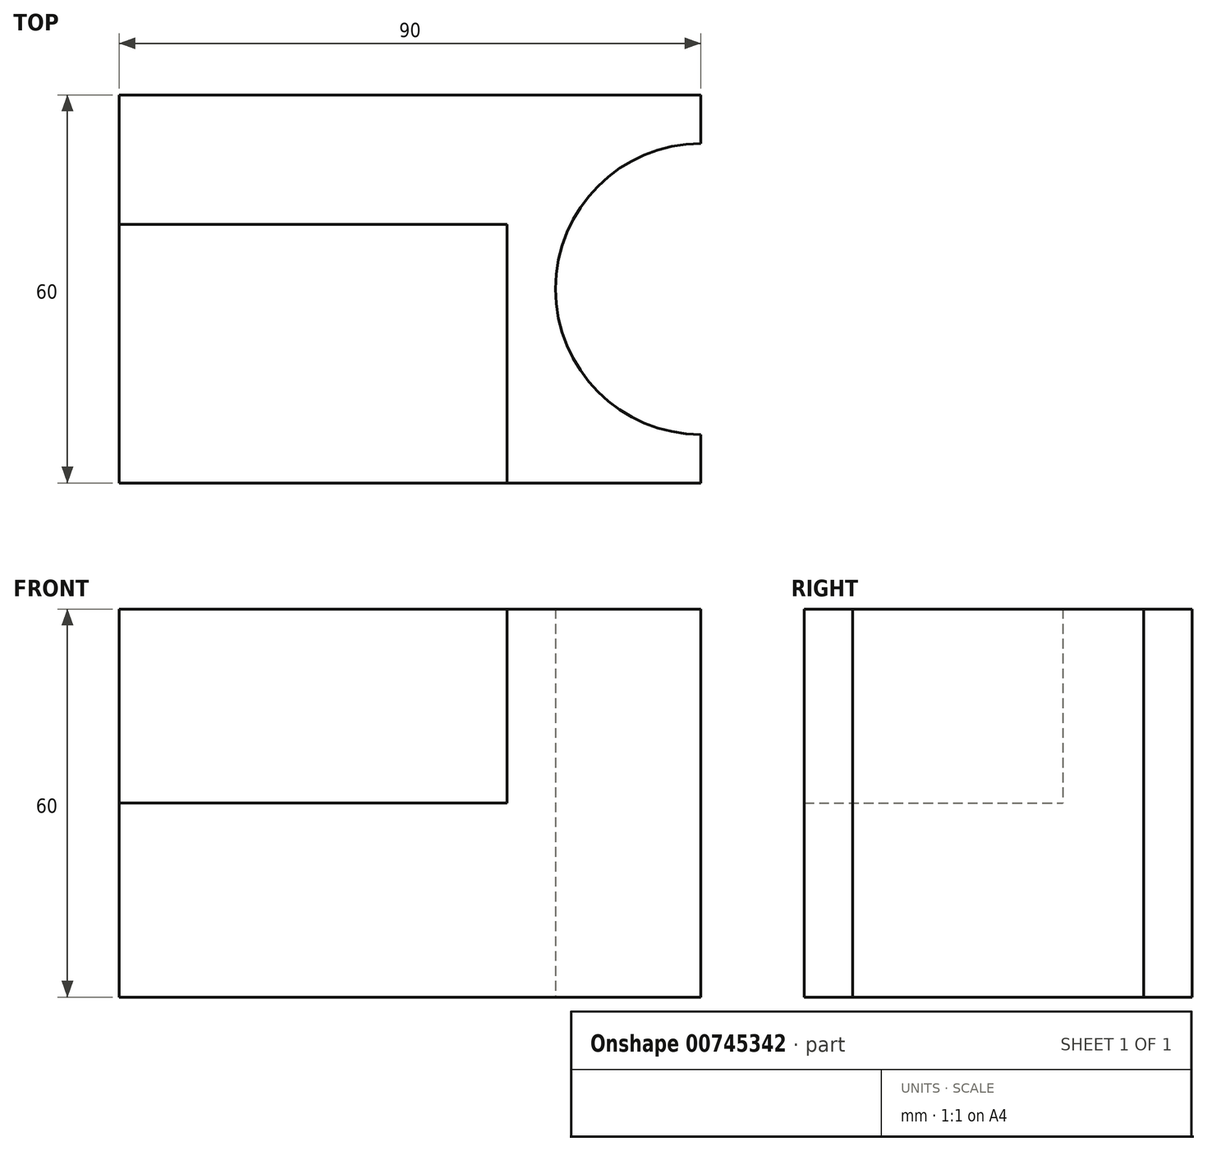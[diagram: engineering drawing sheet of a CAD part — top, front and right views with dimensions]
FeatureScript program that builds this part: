
annotation { "Feature Type Name" : "Feature", "Feature Type Description" : "" }
export const myFeature = defineFeature(function(context is Context, id is Id, definition is map)
    precondition{}
    {
        {
            var Q0;
            Q0=qCreatedBy(makeId("Top.planeOp"),FACE);
            var sketch = newSketch(context, id + "F0", { "sketchPlane" : qUnion([Q0])});
            skLineSegment(sketch, "E0", {"start": v(0, 0) * mm, "end": v(90, 0) * mm});
            skLineSegment(sketch, "E1", {"start": v(90, 0) * mm, "end": v(90, 60) * mm});
            skLineSegment(sketch, "E2", {"start": v(90, 60) * mm, "end": v(0, 60) * mm});
            skLineSegment(sketch, "E3", {"start": v(0, 60) * mm, "end": v(0, 0) * mm});
            skArc(sketch, "E4", {"start": v(90, 52.5) * mm, "mid": v(67.5, 30) * mm, "end": v(90, 7.5) * mm});
            skSolve(sketch);
        }
        {
            var Q0;
            {var subQ3=sQuery(id+"F0.wireOp",EDGE,"E0");Q0=makeQuery(id+"F0.imprint","IMPRINT",FACE,{"disambiguationData":[TD([[makeQuery(id+"F0.imprint","IMPRINT",EDGE,{"derivedFrom":subQ3}),1.0]])]});}
            extrude(context, id + "F1", {"entities" : qUnion([Q0]), "depth" : 30 * mm, "offsetDistance" : 25 * mm});
        }
        {
            var Q0;
            Q0=makeQuery(id+"F1.opExtrude","CAP_FACE",FACE,{"disambiguationData":[OSD([sQuery(id+"F0.wireOp",EDGE,"E0"),sQuery(id+"F0.wireOp",EDGE,"E1"),sQuery(id+"F0.wireOp",EDGE,"E2"),sQuery(id+"F0.wireOp",EDGE,"E3")])],"isStart":false});
            var sketch = newSketch(context, id + "F2", { "sketchPlane" : qUnion([Q0])});
            skLineSegment(sketch, "E5", {"start": v(90, 0) * mm, "end": v(90, 60) * mm});
            skLineSegment(sketch, "E6", {"start": v(90, 60) * mm, "end": v(0, 60) * mm});
            skLineSegment(sketch, "E7", {"start": v(90, 0) * mm, "end": v(60, 0) * mm});
            skLineSegment(sketch, "E8", {"start": v(60, 0) * mm, "end": v(60, 40) * mm});
            skLineSegment(sketch, "E9", {"start": v(60, 40) * mm, "end": v(0, 40) * mm});
            skLineSegment(sketch, "E10", {"start": v(0, 40) * mm, "end": v(0, 60) * mm});
            skArc(sketch, "E11", {"start": v(90, 52.5) * mm, "mid": v(67.5, 30) * mm, "end": v(90, 7.5) * mm});
            skSolve(sketch);
        }
        {
            var Q0;
            {var subQ1=sQuery(id+"F2.wireOp",EDGE,"E6");Q0=makeQuery(id+"F2.imprint","IMPRINT",FACE,{"disambiguationData":[TD([[makeQuery(id+"F2.imprint","IMPRINT",EDGE,{"derivedFrom":subQ1}),1.0]])]});}
            extrude(context, id + "F3", {"entities" : qUnion([Q0]), "operationType" : NewBodyOperationType.ADD, "depth" : 30 * mm, "offsetDistance" : 25 * mm});
        }
    });
